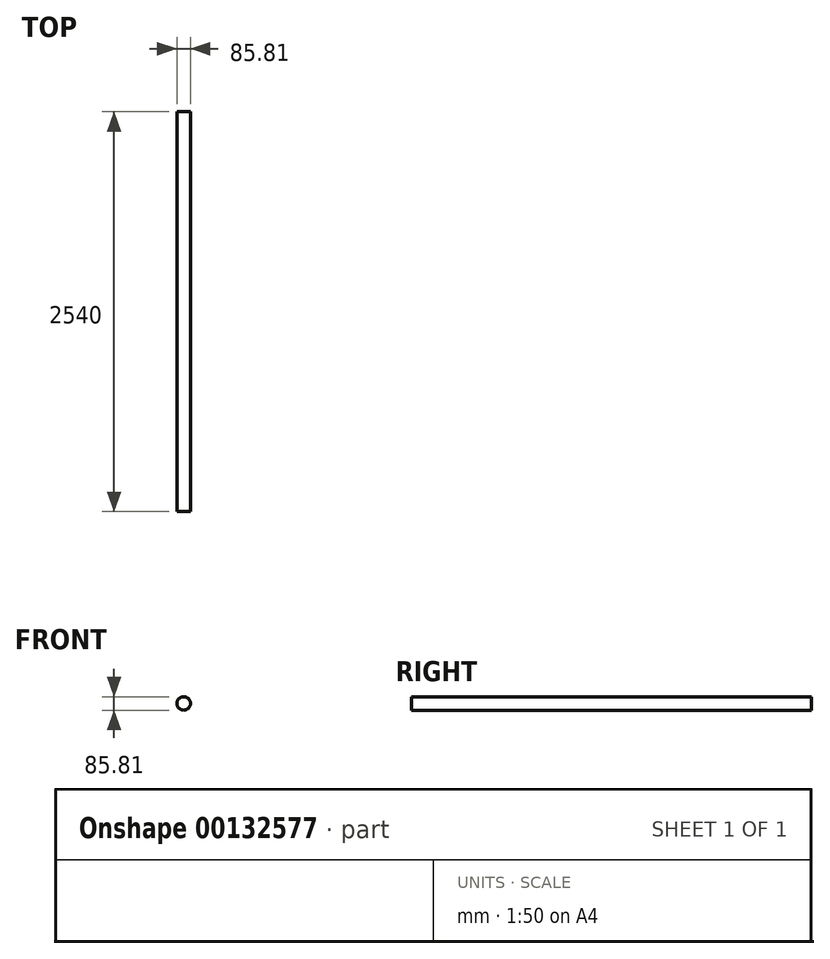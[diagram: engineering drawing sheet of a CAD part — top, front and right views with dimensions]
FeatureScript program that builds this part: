
annotation { "Feature Type Name" : "Feature", "Feature Type Description" : "" }
export const myFeature = defineFeature(function(context is Context, id is Id, definition is map)
    precondition{}
    {
        {
            var Q0;
            Q0=qCreatedBy(makeId("Front.planeOp"),FACE);
            var sketch = newSketch(context, id + "F0", { "sketchPlane" : qUnion([Q0])});
            skCircle(sketch, "E0", {"center": v(2.4, 15.86) * mm, "radius": 42.9 * mm});
            skPoint(sketch, "E0.first.point", {"position": v(-40.23, 20.71) * mm});
            skPoint(sketch, "E0.second.point", {"position": v(36.65, -9.98) * mm});
            skPoint(sketch, "E0.third.point", {"position": v(34.57, 44.25) * mm});
            skSolve(sketch);
        }
        {
            var Q0;
            Q0=makeQuery(id+"F0.imprint","IMPRINT",FACE,{"disambiguationData":[TD([[makeQuery(id+"F0.imprint","IMPRINT",EDGE,{"derivedFrom":sQuery(id+"F0.wireOp",EDGE,"E0")}),1.0]])]});
            extrude(context, id + "F1", {"entities" : qUnion([Q0]), "depth" : 2540 * mm});
        }
    });
